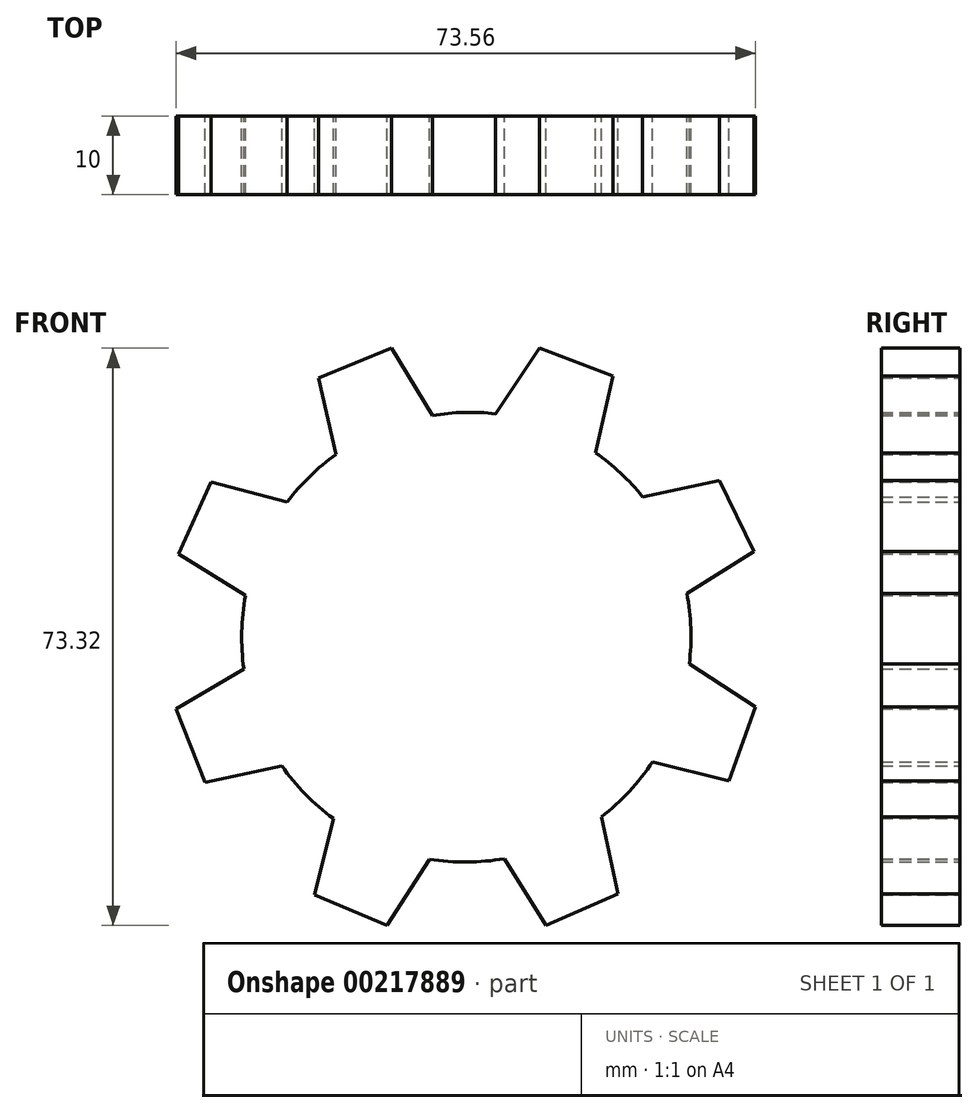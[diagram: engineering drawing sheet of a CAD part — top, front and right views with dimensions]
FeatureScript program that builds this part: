
annotation { "Feature Type Name" : "Feature", "Feature Type Description" : "" }
export const myFeature = defineFeature(function(context is Context, id is Id, definition is map)
    precondition{}
    {
        {
            var Q0;
            Q0=qCreatedBy(makeId("Front.planeOp"),FACE);
            var sketch = newSketch(context, id + "F0", { "sketchPlane" : qUnion([Q0])});
            skLineSegment(sketch, "E0", {"start": v(-38.33, 40.88) * mm, "end": v(37.87, 40.88) * mm});
            skPoint(sketch, "E1", {"position": v(-0.23, 40.88) * mm});
            skPoint(sketch, "E2", {"position": v(-38.33, 2.78) * mm});
            skPoint(sketch, "E3", {"position": v(-0.23, 2.78) * mm});
            skCircle(sketch, "E4", {"center": v(-0.23, 2.78) * mm, "radius": 10.54 * mm});
            skCircle(sketch, "E5", {"center": v(-0.23, 2.78) * mm, "radius": 28.54 * mm});
            skPoint(sketch, "E6", {"position": v(-6.85, 30.55) * mm});
            skPoint(sketch, "E7", {"position": v(6.37, 30.55) * mm});
            skPoint(sketch, "E8", {"position": v(13.84, 27.61) * mm});
            skPoint(sketch, "E9", {"position": v(23.75, 18.25) * mm});
            skPoint(sketch, "E10", {"position": v(27.78, -2.67) * mm});
            skPoint(sketch, "E11", {"position": v(27.16, 10.79) * mm});
            skPoint(sketch, "E12", {"position": v(24.7, -11.11) * mm});
            skPoint(sketch, "E13", {"position": v(15.72, -20.88) * mm});
            skPoint(sketch, "E14", {"position": v(7.12, -24.8) * mm});
            skPoint(sketch, "E15", {"position": v(-6.32, -25.1) * mm});
            skPoint(sketch, "E16", {"position": v(-15.13, -21.56) * mm});
            skPoint(sketch, "E17", {"position": v(-24.52, -12.2) * mm});
            skPoint(sketch, "E18", {"position": v(-28.07, -3.52) * mm});
            skPoint(sketch, "E19", {"position": v(-27.92, 9.7) * mm});
            skPoint(sketch, "E20", {"position": v(-24.22, 18.25) * mm});
            skPoint(sketch, "E21", {"position": v(-14.85, 27.3) * mm});
            skPoint(sketch, "E22", {"position": v(-30.1, 26.34) * mm});
            skPoint(sketch, "E23", {"position": v(-22.88, 33.26) * mm});
            skPoint(sketch, "E24", {"position": v(-5.25, 40.42) * mm});
            skPoint(sketch, "E25", {"position": v(4.75, 40.42) * mm});
            skPoint(sketch, "E26", {"position": v(22.1, 33.25) * mm});
            skPoint(sketch, "E27", {"position": v(29.45, 26.47) * mm});
            skPoint(sketch, "E28", {"position": v(37, 9.02) * mm});
            skPoint(sketch, "E29", {"position": v(37.63, -0.96) * mm});
            skPoint(sketch, "E30", {"position": v(30.43, -19.3) * mm});
            skPoint(sketch, "E31", {"position": v(23.8, -26.78) * mm});
            skPoint(sketch, "E32", {"position": v(5.4, -34.64) * mm});
            skPoint(sketch, "E33", {"position": v(-4.6, -34.95) * mm});
            skPoint(sketch, "E34", {"position": v(-23.3, -27.33) * mm});
            skPoint(sketch, "E35", {"position": v(-30.4, -20.29) * mm});
            skPoint(sketch, "E36", {"position": v(-37.92, -1.82) * mm});
            skPoint(sketch, "E37", {"position": v(-37.8, 8.18) * mm});
            skLineSegment(sketch, "E38", {"start": v(13.84, 27.61) * mm, "end": v(22.1, 33.25) * mm});
            skLineSegment(sketch, "E39", {"start": v(23.75, 18.25) * mm, "end": v(29.45, 26.47) * mm});
            skLineSegment(sketch, "E40", {"start": v(27.16, 10.79) * mm, "end": v(37, 9.02) * mm});
            skLineSegment(sketch, "E41", {"start": v(27.78, -2.67) * mm, "end": v(37.63, -0.96) * mm});
            skLineSegment(sketch, "E42", {"start": v(24.7, -11.11) * mm, "end": v(30.43, -19.3) * mm});
            skLineSegment(sketch, "E43", {"start": v(15.72, -20.88) * mm, "end": v(23.8, -26.78) * mm});
            skLineSegment(sketch, "E44", {"start": v(7.12, -24.8) * mm, "end": v(5.4, -34.64) * mm});
            skLineSegment(sketch, "E45", {"start": v(-6.32, -25.1) * mm, "end": v(-4.6, -34.95) * mm});
            skLineSegment(sketch, "E46", {"start": v(-15.13, -21.56) * mm, "end": v(-23.3, -27.33) * mm});
            skLineSegment(sketch, "E47", {"start": v(-24.52, -12.2) * mm, "end": v(-30.4, -20.29) * mm});
            skLineSegment(sketch, "E48", {"start": v(-28.07, -3.52) * mm, "end": v(-37.92, -1.82) * mm});
            skLineSegment(sketch, "E49", {"start": v(-37.8, 8.18) * mm, "end": v(-27.92, 9.7) * mm});
            skLineSegment(sketch, "E50", {"start": v(-24.22, 18.25) * mm, "end": v(-30.1, 26.34) * mm});
            skLineSegment(sketch, "E51", {"start": v(-22.88, 33.26) * mm, "end": v(-14.85, 27.3) * mm});
            skLineSegment(sketch, "E52", {"start": v(-6.85, 30.55) * mm, "end": v(-5.25, 40.42) * mm});
            skLineSegment(sketch, "E53", {"start": v(4.75, 40.42) * mm, "end": v(6.37, 30.55) * mm});
            skLineSegment(sketch, "E54", {"start": v(-5.25, 40.42) * mm, "end": v(4.75, 40.42) * mm});
            skLineSegment(sketch, "E55", {"start": v(22.1, 33.25) * mm, "end": v(29.45, 26.47) * mm});
            skLineSegment(sketch, "E56", {"start": v(37, 9.02) * mm, "end": v(37.63, -0.96) * mm});
            skLineSegment(sketch, "E57", {"start": v(30.43, -19.3) * mm, "end": v(23.8, -26.78) * mm});
            skLineSegment(sketch, "E58", {"start": v(5.4, -34.64) * mm, "end": v(-4.6, -34.95) * mm});
            skLineSegment(sketch, "E59", {"start": v(-23.3, -27.33) * mm, "end": v(-30.4, -20.29) * mm});
            skLineSegment(sketch, "E60", {"start": v(-37.92, -1.82) * mm, "end": v(-37.8, 8.18) * mm});
            skLineSegment(sketch, "E61", {"start": v(-30.1, 26.34) * mm, "end": v(-22.88, 33.26) * mm});
            skSolve(sketch);
        }
        {
            var Q0;
            Q0=makeQuery(id+"F0.imprint","IMPRINT",FACE,{"disambiguationData":[TD([[makeQuery(id+"F0.imprint","IMPRINT",EDGE,{"derivedFrom":sQuery(id+"F0.wireOp",EDGE,"E4")}),-1.0]])]});
            var Q1;
            {var subQ0=sQuery(id+"F0.wireOp",EDGE,"E50");Q1=makeQuery(id+"F0.imprint","IMPRINT",FACE,{"disambiguationData":[TD([[makeQuery(id+"F0.imprint","IMPRINT",EDGE,{"derivedFrom":subQ0}),-1.0]])]});}
            var Q2;
            {var subQ0=sQuery(id+"F0.wireOp",EDGE,"E48");Q2=makeQuery(id+"F0.imprint","IMPRINT",FACE,{"disambiguationData":[TD([[makeQuery(id+"F0.imprint","IMPRINT",EDGE,{"derivedFrom":subQ0}),-1.0]])]});}
            var Q3;
            {var subQ0=sQuery(id+"F0.wireOp",EDGE,"E46");Q3=makeQuery(id+"F0.imprint","IMPRINT",FACE,{"disambiguationData":[TD([[makeQuery(id+"F0.imprint","IMPRINT",EDGE,{"derivedFrom":subQ0}),-1.0]])]});}
            var Q4;
            {var subQ0=sQuery(id+"F0.wireOp",EDGE,"E44");Q4=makeQuery(id+"F0.imprint","IMPRINT",FACE,{"disambiguationData":[TD([[makeQuery(id+"F0.imprint","IMPRINT",EDGE,{"derivedFrom":subQ0}),-1.0]])]});}
            var Q5;
            {var subQ0=sQuery(id+"F0.wireOp",EDGE,"E42");Q5=makeQuery(id+"F0.imprint","IMPRINT",FACE,{"disambiguationData":[TD([[makeQuery(id+"F0.imprint","IMPRINT",EDGE,{"derivedFrom":subQ0}),-1.0]])]});}
            var Q6;
            {var subQ0=sQuery(id+"F0.wireOp",EDGE,"E40");Q6=makeQuery(id+"F0.imprint","IMPRINT",FACE,{"disambiguationData":[TD([[makeQuery(id+"F0.imprint","IMPRINT",EDGE,{"derivedFrom":subQ0}),-1.0]])]});}
            var Q7;
            {var subQ0=sQuery(id+"F0.wireOp",EDGE,"E38");Q7=makeQuery(id+"F0.imprint","IMPRINT",FACE,{"disambiguationData":[TD([[makeQuery(id+"F0.imprint","IMPRINT",EDGE,{"derivedFrom":subQ0}),-1.0]])]});}
            var Q8;
            {var subQ0=sQuery(id+"F0.wireOp",EDGE,"E52");Q8=makeQuery(id+"F0.imprint","IMPRINT",FACE,{"disambiguationData":[TD([[makeQuery(id+"F0.imprint","IMPRINT",EDGE,{"derivedFrom":subQ0}),-1.0]])]});}
            extrude(context, id + "F1", {"entities" : qUnion([Q0, Q1, Q2, Q3, Q4, Q5, Q6, Q7, Q8]), "depth" : 10 * mm});
        }
        {
            var Q0;
            Q0=makeQuery(id+"F1.opExtrude","CAP_FACE",FACE,{"disambiguationData":[OSD([sQuery(id+"F0.wireOp",EDGE,"E4"),sQuery(id+"F0.wireOp",EDGE,"E5"),sQuery(id+"F0.wireOp",EDGE,"E38"),sQuery(id+"F0.wireOp",EDGE,"E39"),sQuery(id+"F0.wireOp",EDGE,"E40"),sQuery(id+"F0.wireOp",EDGE,"E41"),sQuery(id+"F0.wireOp",EDGE,"E42"),sQuery(id+"F0.wireOp",EDGE,"E43"),sQuery(id+"F0.wireOp",EDGE,"E44"),sQuery(id+"F0.wireOp",EDGE,"E45"),sQuery(id+"F0.wireOp",EDGE,"E46"),sQuery(id+"F0.wireOp",EDGE,"E47"),sQuery(id+"F0.wireOp",EDGE,"E48"),sQuery(id+"F0.wireOp",EDGE,"E49"),sQuery(id+"F0.wireOp",EDGE,"E50"),sQuery(id+"F0.wireOp",EDGE,"E51"),sQuery(id+"F0.wireOp",EDGE,"E52"),sQuery(id+"F0.wireOp",EDGE,"E53"),sQuery(id+"F0.wireOp",EDGE,"E54"),sQuery(id+"F0.wireOp",EDGE,"E55"),sQuery(id+"F0.wireOp",EDGE,"E56"),sQuery(id+"F0.wireOp",EDGE,"E57"),sQuery(id+"F0.wireOp",EDGE,"E58"),sQuery(id+"F0.wireOp",EDGE,"E59"),sQuery(id+"F0.wireOp",EDGE,"E60"),sQuery(id+"F0.wireOp",EDGE,"E61")])],"isStart":false});
            var sketch = newSketch(context, id + "F2", { "sketchPlane" : qUnion([Q0])});
            skArc(sketch, "E62.0", {"start": v(3.95, -13.52) * mm, "mid": v(7.5, -10.3) * mm, "end": v(10.45, -6.53) * mm});
            skArc(sketch, "E62.1", {"start": v(-17.9, -18.91) * mm, "mid": v(-13.14, -19.28) * mm, "end": v(-8.4, -18.84) * mm});
            skArc(sketch, "E62.2", {"start": v(-36.65, -7.05) * mm, "mid": v(-33.66, -10.68) * mm, "end": v(-30.11, -13.76) * mm});
            skArc(sketch, "E62.3", {"start": v(-41.25, 14.58) * mm, "mid": v(-41.75, 9.93) * mm, "end": v(-41.48, 5.26) * mm});
            skArc(sketch, "E62.4", {"start": v(-29.77, 32.5) * mm, "mid": v(-33.1, 29.72) * mm, "end": v(-35.96, 26.48) * mm});
            skArc(sketch, "E62.5", {"start": v(-9.49, 37.67) * mm, "mid": v(-13.5, 37.84) * mm, "end": v(-17.52, 37.45) * mm});
            skArc(sketch, "E62.6", {"start": v(9.17, 27.11) * mm, "mid": v(6.4, 30.13) * mm, "end": v(3.2, 32.71) * mm});
            skArc(sketch, "E63.0", {"start": v(15.1, 5.89) * mm, "mid": v(15.3, 10.4) * mm, "end": v(14.8, 14.87) * mm});
            skLineSegment(sketch, "E64.0", {"start": v(-36.65, -7.05) * mm, "end": v(-46.43, -9.17) * mm});
            skLineSegment(sketch, "E64.1", {"start": v(-50.07, 0.14) * mm, "end": v(-41.48, 5.26) * mm});
            skLineSegment(sketch, "E64.2", {"start": v(-41.25, 14.58) * mm, "end": v(-49.74, 19.87) * mm});
            skLineSegment(sketch, "E64.3", {"start": v(-45.64, 28.99) * mm, "end": v(-35.96, 26.48) * mm});
            skLineSegment(sketch, "E64.4", {"start": v(-29.77, 32.5) * mm, "end": v(-31.99, 42.24) * mm});
            skLineSegment(sketch, "E64.5", {"start": v(-22.72, 46) * mm, "end": v(-17.52, 37.45) * mm});
            skLineSegment(sketch, "E64.6", {"start": v(-9.49, 37.67) * mm, "end": v(-3.95, 46) * mm});
            skLineSegment(sketch, "E64.7", {"start": v(3.2, 32.71) * mm, "end": v(5.4, 42.47) * mm});
            skLineSegment(sketch, "E64.8", {"start": v(9.17, 27.11) * mm, "end": v(18.96, 29.17) * mm});
            skLineSegment(sketch, "E64.9", {"start": v(14.8, 14.87) * mm, "end": v(23.28, 20.16) * mm});
            skLineSegment(sketch, "E64.10", {"start": v(15.1, 5.89) * mm, "end": v(23.5, 0.45) * mm});
            skLineSegment(sketch, "E64.11", {"start": v(10.45, -6.53) * mm, "end": v(20.15, -8.97) * mm});
            skLineSegment(sketch, "E64.12", {"start": v(3.95, -13.52) * mm, "end": v(6.04, -23.3) * mm});
            skLineSegment(sketch, "E64.13", {"start": v(-8.4, -18.84) * mm, "end": v(-3.1, -27.33) * mm});
            skLineSegment(sketch, "E64.14", {"start": v(-17.9, -18.91) * mm, "end": v(-23.3, -27.33) * mm});
            skLineSegment(sketch, "E64.15", {"start": v(-30.11, -13.76) * mm, "end": v(-32.52, -23.47) * mm});
            skLineSegment(sketch, "E65.0", {"start": v(-46.43, -9.17) * mm, "end": v(-50.07, 0.14) * mm});
            skLineSegment(sketch, "E65.1", {"start": v(-23.3, -27.33) * mm, "end": v(-32.52, -23.47) * mm});
            skLineSegment(sketch, "E65.2", {"start": v(6.04, -23.3) * mm, "end": v(-3.1, -27.33) * mm});
            skLineSegment(sketch, "E65.3", {"start": v(23.5, 0.45) * mm, "end": v(20.15, -8.97) * mm});
            skLineSegment(sketch, "E65.4", {"start": v(18.96, 29.17) * mm, "end": v(23.28, 20.16) * mm});
            skLineSegment(sketch, "E65.5", {"start": v(-3.95, 45.86) * mm, "end": v(5.4, 42.33) * mm});
            skLineSegment(sketch, "E65.6", {"start": v(-31.99, 42.24) * mm, "end": v(-22.72, 46) * mm});
            skLineSegment(sketch, "E65.7", {"start": v(-49.74, 19.87) * mm, "end": v(-45.64, 28.99) * mm});
            skLineSegment(sketch, "E65.8", {"start": v(-3.95, 46) * mm, "end": v(5.4, 42.47) * mm});
            skSolve(sketch);
        }
        {
            var Q0;
            Q0=makeQuery(id+"F1.opExtrude","SWEPT_BODY",BODY,{"disambiguationData":[OSD([sQuery(id+"F0.wireOp",EDGE,"E4"),sQuery(id+"F0.wireOp",EDGE,"E5"),sQuery(id+"F0.wireOp",EDGE,"E38"),sQuery(id+"F0.wireOp",EDGE,"E39"),sQuery(id+"F0.wireOp",EDGE,"E40"),sQuery(id+"F0.wireOp",EDGE,"E41"),sQuery(id+"F0.wireOp",EDGE,"E42"),sQuery(id+"F0.wireOp",EDGE,"E43"),sQuery(id+"F0.wireOp",EDGE,"E44"),sQuery(id+"F0.wireOp",EDGE,"E45"),sQuery(id+"F0.wireOp",EDGE,"E46"),sQuery(id+"F0.wireOp",EDGE,"E47"),sQuery(id+"F0.wireOp",EDGE,"E48"),sQuery(id+"F0.wireOp",EDGE,"E49"),sQuery(id+"F0.wireOp",EDGE,"E50"),sQuery(id+"F0.wireOp",EDGE,"E51"),sQuery(id+"F0.wireOp",EDGE,"E52"),sQuery(id+"F0.wireOp",EDGE,"E53"),sQuery(id+"F0.wireOp",EDGE,"E54"),sQuery(id+"F0.wireOp",EDGE,"E55"),sQuery(id+"F0.wireOp",EDGE,"E56"),sQuery(id+"F0.wireOp",EDGE,"E57"),sQuery(id+"F0.wireOp",EDGE,"E58"),sQuery(id+"F0.wireOp",EDGE,"E59"),sQuery(id+"F0.wireOp",EDGE,"E60"),sQuery(id+"F0.wireOp",EDGE,"E61")])]});
            deleteBodies(context, id + "F3", {"entities" : qUnion([Q0])});
        }
        {
            var Q0;
            Q0=makeQuery(id+"F2.imprint","IMPRINT",FACE,{"disambiguationData":[TD([[makeQuery(id+"F2.imprint","IMPRINT",EDGE,{"derivedFrom":sQuery(id+"F2.wireOp",EDGE,"E62.2")}),1.0]])]});
            var Q1;
            Q1=makeQuery(id+"F2.imprint","IMPRINT",FACE,{"disambiguationData":[TD([[makeQuery(id+"F2.imprint","IMPRINT",EDGE,{"derivedFrom":sQuery(id+"F2.wireOp",EDGE,"E62.0")}),1.0]])]});
            var Q2;
            Q2=makeQuery(id+"F2.imprint","IMPRINT",FACE,{"disambiguationData":[TD([[makeQuery(id+"F2.imprint","IMPRINT",EDGE,{"derivedFrom":makeQuery(id+"F1.opExtrude","CAP_EDGE",EDGE,{"disambiguationData":[OSD([sQuery(id+"F0.wireOp",EDGE,"E4")])],"isStart":false})}),1.0]])]});
            var Q3;
            {var subQ0=sQuery(id+"F2.wireOp",EDGE,"E64.8");var subQ1=sQuery(id+"F0.wireOp",EDGE,"E38");var subQ5=makeQuery(id+"F1.opExtrude","CAP_EDGE",EDGE,{"disambiguationData":[OSD([subQ1])],"isStart":false});var subQ6=makeQuery(id+"F2.imprint","INTERSECT",VERTEX,{"derivedFrom":[subQ5,subQ0]});Q3=makeQuery(id+"F2.imprint","IMPRINT",FACE,{"disambiguationData":[TD([[makeQuery(id+"F2.imprint","IMPRINT",EDGE,{"disambiguationData":[TD([[subQ6,1.0]])],"derivedFrom":subQ0}),-1.0]])]});}
            extrude(context, id + "F4", {"entities" : qUnion([Q0, Q1, Q2, Q3]), "depth" : 10 * mm});
        }
    });
